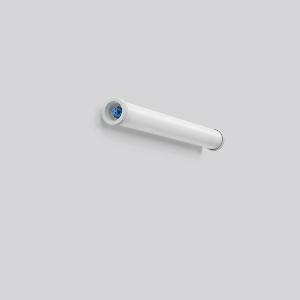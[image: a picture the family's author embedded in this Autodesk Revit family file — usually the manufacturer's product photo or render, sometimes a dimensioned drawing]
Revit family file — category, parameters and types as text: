
# Revit family: planox_tube_farm_601070_002_5_b502
name_source: partatom
category: Lighting Fixtures
units: mm (PartAtom-declared; Revit-internal decimal feet)

## family parameters
Cut with Voids When Loaded = No
Host = Face
Light Source = No
Part Type = Normal
Room Calculation Point = No
Round Connector Dimension = Use Diameter
Shared = No

## types (1)
- PLANOX TUBE FARM (1 x LED Modul 840, 4050 lm, 4000)
    Apparent Load = 31 VA
    CIE Flux Codes = 44 74 91 91 100
    Color Rendering = 80
    Color Temperature = 4000
    Default Elevation = 1800 mm
    Description = Series: PLANOX TUBE FARM
Ammonia-resistant protective tube luminaire for tough requirements. Rack made of sheet steel, white powder coated. End caps made of plastic (polyamide) grey. Diffuser made of UV-resistant plastic (PMMA), opal. Symmetrical light distribution. Homogeneous light distribution. With accessories for wall, ceiling or pendant mounting. Driver integrated. Easy installation with the Plug+Play Wieland RST CLASSIC plug-in system. Mounting set must be ordered separately. Luminaire with limited surface temperature in accordance with EN 60598-2-24 for use in environments in which a deposit of conductive dust on the luminaire can be expected. Ammonia resistant : Suitable for the use in stables with livestock and agricultural side areas. Environmentally friendly and resource-saving due to replaceable components. 
Colour: white
Diameter: 78 mm
Length: 722 mm
Lamp: LED
Socket: without socket
Colour temperature: 4000K
Colour rendering index (CRI): 83
System power: 31 W
Rated luminous flux: 4050 lm
Luminous efficiency: 131 lm/W
Control gear: Regulated power supply
Protection class: I
Type of protection: IP 67
    Height = 0 mm  [stored 0 ft]
    Lamp = 1 x LED Modul 840
    Lamp Light Flux = 4050 lm
    Lamp count = 1
    Length = 722 mm
    Lifetime = 50000 h
    Luminous efficacy = 131 lm/W
    Manufacturer = RZB
    ModVariant = No
    Model = 601070.002.5
    Mounting Place = Ceiling
    Mounting Type = Surface mounted
    Number of Poles = 1
    OnlyDefault = Yes
    Power Factor = 1
    Product Name = PLANOX TUBE FARM
    Product group = Surface mounted luminaires for moist/humid enviroments
    ProductGroupID = 308
    Protection Class = Protection class I
    Protection Degree = Degree of protection
    RLX_Detail_Level = 1
    RLX_Emergency_Light_Flux = 0 lm
    RLX_Emergency_Type = 0
    RLX_Emergency_Type_DB = No
    RlxData = <blob elided: 31261 chars, md5=f0010442>
    Socket = socket
    Standby Power = 0 W
    System Light Flux = 4050 lm
    System Power = 31 W
    Type Comments = Product without accessories
    Type Image = 601070.002.5.jpg
    URL = http://relux.com
    VarID = ---
    Voltage = 0 V
    Weight = 0.00 kg
    Width = 0 mm  [stored 0 ft]

note: [stored X ft] marks values corroborated as IEEE doubles in the binary element streams (Revit-internal decimal feet)

## geometry (parser evidence)
native form markers: Blend x4, Sweep x12
no freeform markers — native parametric forms only
